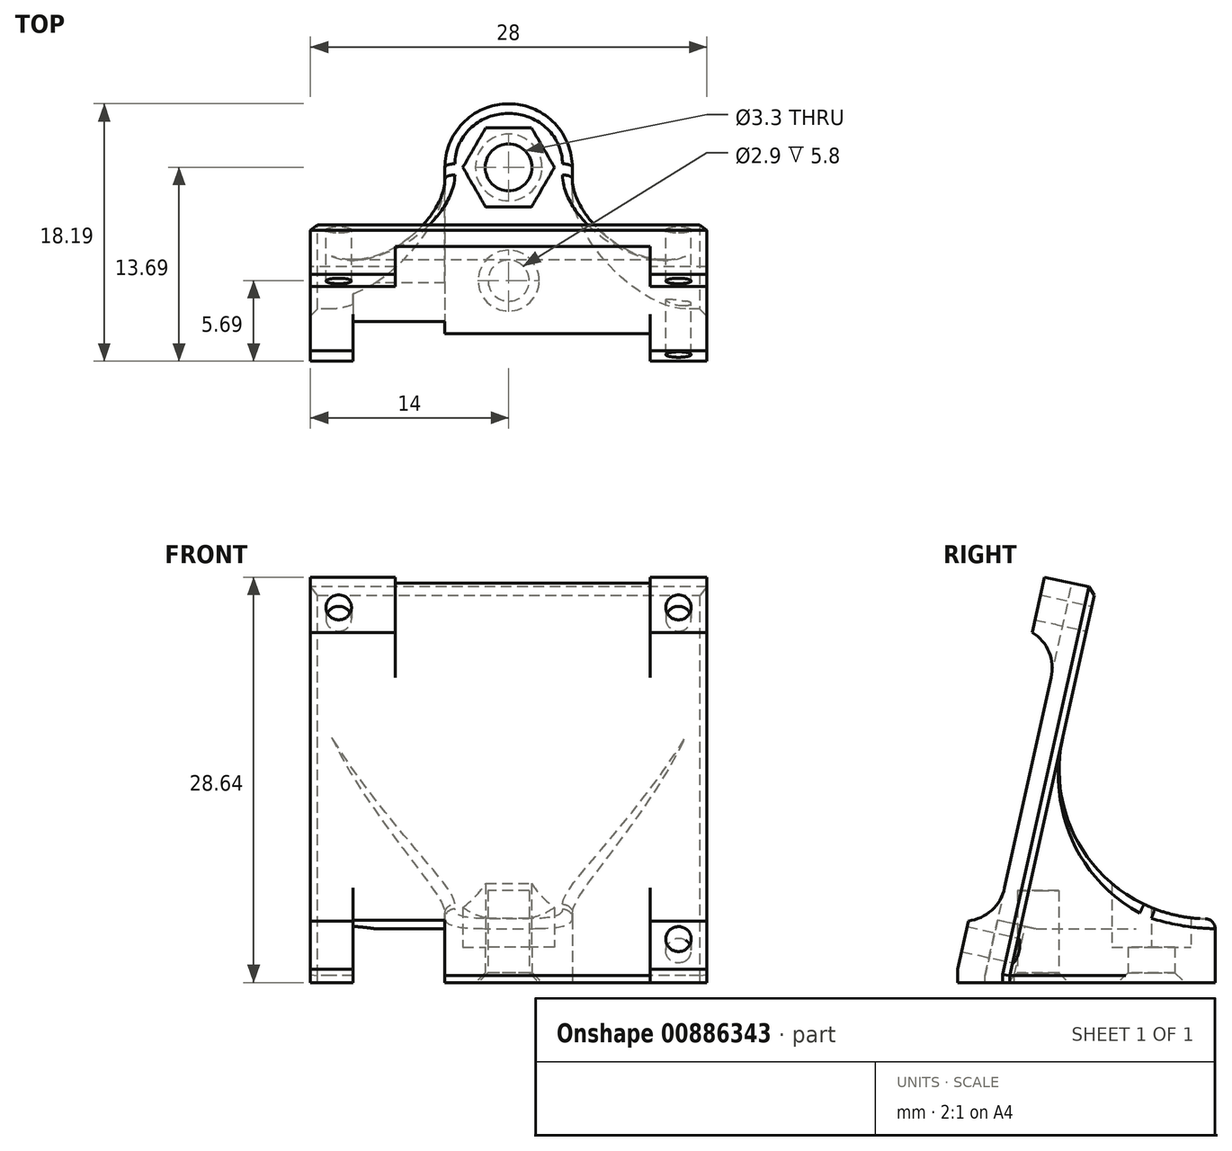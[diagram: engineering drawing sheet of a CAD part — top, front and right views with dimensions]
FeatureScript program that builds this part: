
annotation { "Feature Type Name" : "Feature", "Feature Type Description" : "" }
export const myFeature = defineFeature(function(context is Context, id is Id, definition is map)
    precondition{}
    {
        {
            var Q0;
            Q0=qCreatedBy(makeId("Top.planeOp"),FACE);
            var sketch = newSketch(context, id + "F0", { "sketchPlane" : qUnion([Q0])});
            skCircle(sketch, "E0", {"center": v(0, 0) * mm, "radius": 1.65 * mm});
            skCircle(sketch, "E1.cCircle", {"center": v(0, 0) * mm, "radius": 2.8 * mm, "construction": true});
            skLineSegment(sketch, "E1.0", {"start": v(-1.62, 2.8) * mm, "end": v(1.62, 2.8) * mm});
            skLineSegment(sketch, "E1.1", {"start": v(1.62, 2.8) * mm, "end": v(3.23, 0) * mm});
            skLineSegment(sketch, "E1.2", {"start": v(3.23, 0) * mm, "end": v(1.62, -2.8) * mm});
            skLineSegment(sketch, "E1.3", {"start": v(1.62, -2.8) * mm, "end": v(-1.62, -2.8) * mm});
            skLineSegment(sketch, "E1.4", {"start": v(-1.62, -2.8) * mm, "end": v(-3.23, 0) * mm});
            skLineSegment(sketch, "E1.5", {"start": v(-3.23, 0) * mm, "end": v(-1.62, 2.8) * mm});
            skPoint(sketch, "E1.0.midPoint", {"position": v(0, 2.8) * mm});
            skCircle(sketch, "E2", {"center": v(0, 0) * mm, "radius": 4.5 * mm});
            skLineSegment(sketch, "E3", {"start": v(-4.5, 0) * mm, "end": v(-4.5, -10) * mm});
            skLineSegment(sketch, "E4", {"start": v(-4.5, -10) * mm, "end": v(4.5, -10) * mm});
            skLineSegment(sketch, "E5", {"start": v(4.5, -10) * mm, "end": v(4.5, 0) * mm});
            skCircle(sketch, "E6", {"center": v(0, -8) * mm, "radius": 1.45 * mm});
            skSolve(sketch);
        }
        {
            var Q0;
            Q0 = qSketchRegion(id + "F0", true);
            var Q1;
            Q1=makeQuery(id+"F0.imprint","IMPRINT",FACE,{"disambiguationData":[TD([[makeQuery(id+"F0.imprint","IMPRINT",EDGE,{"derivedFrom":sQuery(id+"F0.wireOp",EDGE,"E0")}),-1.0]])]});
            var Q2;
            Q2=makeQuery(id+"F0.imprint","IMPRINT",FACE,{"disambiguationData":[TD([[makeQuery(id+"F0.imprint","IMPRINT",EDGE,{"derivedFrom":sQuery(id+"F0.wireOp",EDGE,"E6")}),1.0]])]});
            extrude(context, id + "F1", {"entities" : qUnion([Q0, Q1, Q2]), "depth" : 4 * mm, "offsetDistance" : 25 * mm});
        }
        {
            var Q0;
            Q0=qCreatedBy(makeId("Right.planeOp"),FACE);
            var sketch = newSketch(context, id + "F2", { "sketchPlane" : qUnion([Q0])});
            skPoint(sketch, "E7.0", {"position": v(-10, 0) * mm});
            skLineSegment(sketch, "E8", {"start": v(-10, 0) * mm, "end": v(-3.94, 27.34) * mm});
            skLineSegment(sketch, "E9", {"start": v(-3.94, 27.34) * mm, "end": v(-5.6, 27.7) * mm});
            skLineSegment(sketch, "E10", {"start": v(-5.6, 27.7) * mm, "end": v(-11.74, 0) * mm});
            skLineSegment(sketch, "E11", {"start": v(-11.74, 0) * mm, "end": v(-10, 0) * mm});
            skLineSegment(sketch, "E12", {"start": v(-11.74, 0) * mm, "end": v(-13.7, 0.43) * mm});
            skLineSegment(sketch, "E13", {"start": v(-13.7, 0.43) * mm, "end": v(-13.7, 0) * mm});
            skLineSegment(sketch, "E14", {"start": v(-13.7, 0) * mm, "end": v(-11.74, 0) * mm});
            skSolve(sketch);
        }
        {
            var Q0;
            Q0=makeQuery(id+"F2.imprint","IMPRINT",FACE,{"disambiguationData":[TD([[makeQuery(id+"F2.imprint","IMPRINT",EDGE,{"derivedFrom":sQuery(id+"F2.wireOp",EDGE,"E8")}),1.0]])]});
            extrude(context, id + "F3", {"entities" : qUnion([Q0]), "operationType" : NewBodyOperationType.ADD, "endBound" : BoundingType.SYMMETRIC, "depth" : 28 * mm, "offsetDistance" : 25 * mm});
        }
        {
            var Q0;
            Q0=makeQuery(id+"F0.imprint","IMPRINT",FACE,{"disambiguationData":[TD([[makeQuery(id+"F0.imprint","IMPRINT",EDGE,{"derivedFrom":sQuery(id+"F0.wireOp",EDGE,"E0")}),-1.0]])]});
            extrude(context, id + "F4", {"entities" : qUnion([Q0]), "operationType" : NewBodyOperationType.REMOVE, "endBound" : BoundingType.UP_TO_NEXT, "depth" : 6.3 * mm, "offsetDistance" : 25 * mm, "hasSecondDirection" : true, "secondDirectionOppositeDirection" : false, "secondDirectionDepth" : 2 * mm});
        }
        {
            var Q0;
            Q0=makeQuery(id+"F3.opExtrude","SWEPT_FACE",FACE,{"disambiguationData":[OSD([sQuery(id+"F2.wireOp",EDGE,"E10")])]});
            var sketch = newSketch(context, id + "F5", { "sketchPlane" : qUnion([Q0])});
            skLineSegment(sketch, "E15", {"start": v(14, 0.96) * mm, "end": v(10, 0.96) * mm});
            skLineSegment(sketch, "E16", {"start": v(10, 0.96) * mm, "end": v(10, -2.54) * mm});
            skLineSegment(sketch, "E17", {"start": v(-11, -2.54) * mm, "end": v(-11, 0.96) * mm});
            skLineSegment(sketch, "E18", {"start": v(-11, 0.96) * mm, "end": v(-14, 0.96) * mm});
            skLineSegment(sketch, "E19", {"start": v(-4.5, -2.54) * mm, "end": v(-4.5, 1.46) * mm});
            skLineSegment(sketch, "E20", {"start": v(-4.5, 1.46) * mm, "end": v(-11, 1.46) * mm});
            skLineSegment(sketch, "E21", {"start": v(-11, 1.46) * mm, "end": v(-11, 0.96) * mm});
            skLineSegment(sketch, "E22", {"start": v(14, 21.84) * mm, "end": v(10, 21.84) * mm});
            skLineSegment(sketch, "E23", {"start": v(10, 21.84) * mm, "end": v(10, 25.84) * mm});
            skLineSegment(sketch, "E24", {"start": v(-8, 21.84) * mm, "end": v(-8, 25.84) * mm});
            skLineSegment(sketch, "E25.trimOffspring", {"start": v(-8, 21.84) * mm, "end": v(-14, 21.84) * mm});
            skLineSegment(sketch, "E26", {"start": v(0, 25.84) * mm, "end": v(0, -2.54) * mm, "construction": true});
            skLineSegment(sketch, "E27", {"start": v(-14, 11.65) * mm, "end": v(14, 11.65) * mm, "construction": true});
            skPoint(sketch, "E28.middle", {"position": v(0, 11.65) * mm});
            skLineSegment(sketch, "E29.bottom", {"start": v(12, 23.65) * mm, "end": v(-12, 23.65) * mm, "construction": true});
            skLineSegment(sketch, "E29.top", {"start": v(12, -0.35) * mm, "end": v(-12, -0.35) * mm, "construction": true});
            skLineSegment(sketch, "E29.left", {"start": v(12, 23.65) * mm, "end": v(12, -0.35) * mm, "construction": true});
            skLineSegment(sketch, "E29.right", {"start": v(-12, 23.65) * mm, "end": v(-12, -0.35) * mm, "construction": true});
            skCircle(sketch, "E30", {"center": v(12, -0.35) * mm, "radius": 0.9 * mm});
            skCircle(sketch, "E31", {"center": v(12, 23.65) * mm, "radius": 0.9 * mm});
            skCircle(sketch, "E32", {"center": v(-12, 23.65) * mm, "radius": 0.9 * mm});
            skSolve(sketch);
        }
        {
            var Q0;
            {var subQ5=sQuery(id+"F5.wireOp",EDGE,"E24");Q0=makeQuery(id+"F5.imprint","IMPRINT",FACE,{"disambiguationData":[TD([[makeQuery(id+"F5.imprint","IMPRINT",EDGE,{"derivedFrom":subQ5}),1.0]])]});}
            var Q1;
            {var subQ5=sQuery(id+"F5.wireOp",EDGE,"E22");Q1=makeQuery(id+"F5.imprint","IMPRINT",FACE,{"disambiguationData":[TD([[makeQuery(id+"F5.imprint","IMPRINT",EDGE,{"derivedFrom":subQ5}),-1.0]])]});}
            var Q2;
            {var subQ5=sQuery(id+"F5.wireOp",EDGE,"E15");Q2=makeQuery(id+"F5.imprint","IMPRINT",FACE,{"disambiguationData":[TD([[makeQuery(id+"F5.imprint","IMPRINT",EDGE,{"derivedFrom":subQ5}),1.0]])]});}
            var Q3;
            {var subQ0=sQuery(id+"F5.wireOp",EDGE,"E17");Q3=makeQuery(id+"F5.imprint","IMPRINT",FACE,{"disambiguationData":[TD([[makeQuery(id+"F5.imprint","IMPRINT",EDGE,{"derivedFrom":subQ0}),1.0]])]});}
            extrude(context, id + "F6", {"entities" : qUnion([Q0, Q1, Q2, Q3]), "operationType" : NewBodyOperationType.ADD, "depth" : 2 * mm, "offsetDistance" : 25 * mm});
        }
        {
            var Q0;
            {var subQ1=sQuery(id+"F5.wireOp",EDGE,"E17");Q0=makeQuery(id+"F5.imprint","IMPRINT",FACE,{"disambiguationData":[TD([[makeQuery(id+"F5.imprint","IMPRINT",EDGE,{"derivedFrom":subQ1}),-1.0]])]});}
            extrude(context, id + "F7", {"entities" : qUnion([Q0]), "operationType" : NewBodyOperationType.REMOVE, "endBound" : BoundingType.UP_TO_NEXT, "oppositeDirection" : true, "depth" : 25 * mm, "offsetDistance" : 25 * mm});
        }
        {
            var Q0;
            Q0=makeQuery(id+"F3.boolean.opBoolean","INTERSECT",EDGE,{"derivedFrom":[makeQuery(id+"F1.opExtrude","SWEPT_FACE",FACE,{"disambiguationData":[OSD([sQuery(id+"F0.wireOp",EDGE,"E5")])]}),makeQuery(id+"F3.opExtrude","SWEPT_FACE",FACE,{"disambiguationData":[OSD([sQuery(id+"F2.wireOp",EDGE,"E8")])]})]});
            var Q1;
            Q1=makeQuery(id+"F3.boolean.opBoolean","INTERSECT",EDGE,{"derivedFrom":[makeQuery(id+"F1.opExtrude","SWEPT_FACE",FACE,{"disambiguationData":[OSD([sQuery(id+"F0.wireOp",EDGE,"E3")])]}),makeQuery(id+"F3.opExtrude","SWEPT_FACE",FACE,{"disambiguationData":[OSD([sQuery(id+"F2.wireOp",EDGE,"E8")])]})]});
            fillet(context, id + "F8", {"entities" : qUnion([Q0, Q1]), "radius" : 8 * mm, "tangentPropagation" : true, "rho" : 0.3, "crossSection" : FilletCrossSection.CONIC, "allowEdgeOverflow" : false});
        }
        {
            var Q0;
            Q0=makeQuery(id+"F5.imprint","IMPRINT",FACE,{"disambiguationData":[TD([[makeQuery(id+"F5.imprint","IMPRINT",EDGE,{"derivedFrom":sQuery(id+"F5.wireOp",EDGE,"E32")}),1.0]])]});
            var Q1;
            Q1=makeQuery(id+"F5.imprint","IMPRINT",FACE,{"disambiguationData":[TD([[makeQuery(id+"F5.imprint","IMPRINT",EDGE,{"derivedFrom":sQuery(id+"F5.wireOp",EDGE,"E31")}),1.0]])]});
            var Q2;
            Q2=makeQuery(id+"F5.imprint","IMPRINT",FACE,{"disambiguationData":[TD([[makeQuery(id+"F5.imprint","IMPRINT",EDGE,{"derivedFrom":sQuery(id+"F5.wireOp",EDGE,"E30")}),1.0]])]});
            extrude(context, id + "F9", {"entities" : qUnion([Q0, Q1, Q2]), "operationType" : NewBodyOperationType.REMOVE, "endBound" : BoundingType.UP_TO_NEXT, "oppositeDirection" : true, "depth" : 25 * mm, "offsetDistance" : 25 * mm});
        }
        {
            var Q0;
            Q0=makeQuery(id+"F3.boolean.opBoolean","INTERSECT",EDGE,{"derivedFrom":[makeQuery(id+"F1.opExtrude","CAP_FACE",FACE,{"disambiguationData":[OSD([sQuery(id+"F0.wireOp",EDGE,"E0"),sQuery(id+"F0.wireOp",EDGE,"E2"),sQuery(id+"F0.wireOp",EDGE,"E3"),sQuery(id+"F0.wireOp",EDGE,"E4"),sQuery(id+"F0.wireOp",EDGE,"E5")])],"isStart":false}),makeQuery(id+"F3.opExtrude","SWEPT_FACE",FACE,{"disambiguationData":[OSD([sQuery(id+"F2.wireOp",EDGE,"E8")])]})]});
            fillet(context, id + "F10", {"entities" : qUnion([Q0]), "radius" : 10.54 * mm, "tangentPropagation" : true, "allowEdgeOverflow" : false});
        }
        {
            var Q0;
            Q0=makeQuery(id+"F0.imprint","IMPRINT",FACE,{"disambiguationData":[TD([[makeQuery(id+"F0.imprint","IMPRINT",EDGE,{"derivedFrom":sQuery(id+"F0.wireOp",EDGE,"E6")}),1.0]])]});
            extrude(context, id + "F11", {"entities" : qUnion([Q0]), "operationType" : NewBodyOperationType.REMOVE, "depth" : 6 * mm, "offsetDistance" : 25 * mm});
        }
        {
            var Q0;
            Q0=makeQuery(id+"F6.opExtrude","CAP_EDGE",EDGE,{"disambiguationData":[OSD([sQuery(id+"F5.wireOp",EDGE,"E22")])],"isStart":true});
            var Q1;
            Q1=makeQuery(id+"F6.opExtrude","CAP_EDGE",EDGE,{"disambiguationData":[OSD([sQuery(id+"F5.wireOp",EDGE,"E25.trimOffspring")])],"isStart":true});
            var Q2;
            Q2=makeQuery(id+"F6.opExtrude","CAP_EDGE",EDGE,{"disambiguationData":[OSD([sQuery(id+"F5.wireOp",EDGE,"E15")])],"isStart":true});
            var Q3;
            Q3=makeQuery(id+"F6.opExtrude","CAP_EDGE",EDGE,{"disambiguationData":[OSD([sQuery(id+"F5.wireOp",EDGE,"E18")])],"isStart":true});
            fillet(context, id + "F12", {"entities" : qUnion([Q0, Q1, Q2, Q3]), "radius" : 3 * mm, "tangentPropagation" : true, "allowEdgeOverflow" : false});
        }
        {
            var Q0;
            Q0=makeQuery(id+"F2.imprint","IMPRINT",FACE,{"disambiguationData":[TD([[makeQuery(id+"F2.imprint","IMPRINT",EDGE,{"derivedFrom":sQuery(id+"F2.wireOp",EDGE,"E12")}),1.0]])]});
            extrude(context, id + "F13", {"entities" : qUnion([Q0]), "operationType" : NewBodyOperationType.ADD, "depth" : 14 * mm, "offsetDistance" : 25 * mm, "hasSecondDirection" : true, "secondDirectionOppositeDirection" : false, "secondDirectionDepth" : 10 * mm});
        }
        {
            var Q0;
            Q0=makeQuery(id+"F2.imprint","IMPRINT",FACE,{"disambiguationData":[TD([[makeQuery(id+"F2.imprint","IMPRINT",EDGE,{"derivedFrom":sQuery(id+"F2.wireOp",EDGE,"E12")}),1.0]])]});
            extrude(context, id + "F14", {"entities" : qUnion([Q0]), "operationType" : NewBodyOperationType.ADD, "oppositeDirection" : true, "depth" : 14 * mm, "offsetDistance" : 25 * mm, "hasSecondDirection" : true, "secondDirectionOppositeDirection" : true, "secondDirectionDepth" : 11 * mm});
        }
        {
            var Q0;
            {var subQ0=sQuery(id+"F2.wireOp",EDGE,"E8");var subQ1=sQuery(id+"F0.wireOp",EDGE,"E5");Q0=makeQuery(id+"F10.opFillet","BLEND_EDGE",EDGE,{"blendedFrom":[makeQuery(id+"F3.boolean.opBoolean","INTERSECT",EDGE,{"derivedFrom":[makeQuery(id+"F1.opExtrude","CAP_FACE",FACE,{"disambiguationData":[OSD([sQuery(id+"F0.wireOp",EDGE,"E0"),sQuery(id+"F0.wireOp",EDGE,"E2"),sQuery(id+"F0.wireOp",EDGE,"E3"),sQuery(id+"F0.wireOp",EDGE,"E4"),subQ1])],"isStart":false}),makeQuery(id+"F3.opExtrude","SWEPT_FACE",FACE,{"disambiguationData":[OSD([subQ0])]})]}),makeQuery(id+"F8.opFillet","BLEND_FACE",FACE,{"disambiguationData":[OSD([subQ1,subQ0]),OD(0.0)]})],"blendedInto":[makeQuery(id+"F8.opFillet","BLEND_FACE",FACE,{"disambiguationData":[OSD([subQ1,subQ0]),OD(0.0)]})]});}
            fillet(context, id + "F15", {"entities" : qUnion([Q0]), "radius" : 0.7 * mm, "tangentPropagation" : true, "allowEdgeOverflow" : false});
        }
        {
            var Q0;
            {var subQ0=sQuery(id+"F2.wireOp",EDGE,"E14");var subQ3=sQuery(id+"F0.wireOp",EDGE,"E3");var subQ4=sQuery(id+"F0.wireOp",EDGE,"E0");var subQ7=sQuery(id+"F2.wireOp",EDGE,"E11");var subQ12=sQuery(id+"F0.wireOp",EDGE,"E5");var subQ13=sQuery(id+"F0.wireOp",EDGE,"E2");Q0=makeQuery(id+"F13.boolean.opBoolean","MERGE",FACE,{"derivedFrom":[makeQuery(id+"F7.boolean.opBoolean","SPLIT",FACE,{"disambiguationData":[TD([makeQuery(id+"F1.opExtrude","SWEPT_FACE",FACE,{"disambiguationData":[OSD([subQ4])]})])],"derivedFrom":makeQuery(id+"F3.boolean.opBoolean","MERGE",FACE,{"derivedFrom":[makeQuery(id+"F1.opExtrude","CAP_FACE",FACE,{"disambiguationData":[OSD([subQ4,subQ13,subQ3,sQuery(id+"F0.wireOp",EDGE,"E4"),subQ12])],"isStart":true}),makeQuery(id+"F3.opExtrude","SWEPT_FACE",FACE,{"disambiguationData":[OSD([subQ7])]})]})}),makeQuery(id+"F13.opExtrude","SWEPT_FACE",FACE,{"disambiguationData":[OSD([subQ0])]})]});}
            var Q1;
            {var subQ0=sQuery(id+"F2.wireOp",EDGE,"E14");var subQ4=sQuery(id+"F2.wireOp",EDGE,"E11");var subQ7=sQuery(id+"F5.wireOp",EDGE,"E17");Q1=makeQuery(id+"F14.boolean.opBoolean","MERGE",FACE,{"derivedFrom":[makeQuery(id+"F7.boolean.opBoolean","SPLIT",FACE,{"disambiguationData":[TD([makeQuery(id+"F6.opExtrude","SWEPT_FACE",FACE,{"disambiguationData":[OSD([subQ7])]})])],"derivedFrom":makeQuery(id+"F3.boolean.opBoolean","MERGE",FACE,{"derivedFrom":[makeQuery(id+"F1.opExtrude","CAP_FACE",FACE,{"disambiguationData":[OSD([sQuery(id+"F0.wireOp",EDGE,"E0"),sQuery(id+"F0.wireOp",EDGE,"E2"),sQuery(id+"F0.wireOp",EDGE,"E3"),sQuery(id+"F0.wireOp",EDGE,"E4"),sQuery(id+"F0.wireOp",EDGE,"E5")])],"isStart":true}),makeQuery(id+"F3.opExtrude","SWEPT_FACE",FACE,{"disambiguationData":[OSD([subQ4])]})]})}),makeQuery(id+"F14.opExtrude","SWEPT_FACE",FACE,{"disambiguationData":[OSD([subQ0])]})]});}
            extrude(context, id + "F16", {"entities" : qUnion([Q0, Q1]), "operationType" : NewBodyOperationType.ADD, "depth" : 0.5 * mm, "offsetDistance" : 25 * mm});
        }
        {
            var Q0;
            Q0=makeQuery(id+"F16.opExtrude","CAP_EDGE",EDGE,{"disambiguationData":[OSD([sQuery(id+"F0.wireOp",EDGE,"E0")])],"isStart":false});
            var Q1;
            Q1=makeQuery(id+"F16.opExtrude","CAP_EDGE",EDGE,{"disambiguationData":[OSD([sQuery(id+"F0.wireOp",EDGE,"E6")])],"isStart":false});
            chamfer(context, id + "F17", {"entities" : qUnion([Q0, Q1]), "width" : 0.7 * mm, "tangentPropagation" : true});
        }
        {
            var Q0;
            Q0=makeQuery(id+"F3.opExtrude","CAP_EDGE",EDGE,{"disambiguationData":[OSD([sQuery(id+"F2.wireOp",EDGE,"E8")])],"isStart":false});
            var Q1;
            Q1=makeQuery(id+"F3.opExtrude","SWEPT_EDGE",EDGE,{"disambiguationData":[OSD([sQuery(id+"F2.wireOp",EDGE,"E8"),sQuery(id+"F2.wireOp",EDGE,"E9")])]});
            var Q2;
            Q2=makeQuery(id+"F3.opExtrude","CAP_EDGE",EDGE,{"disambiguationData":[OSD([sQuery(id+"F2.wireOp",EDGE,"E8")])],"isStart":true});
            var Q3;
            {var subQ0=sQuery(id+"F2.wireOp",EDGE,"E11");var subQ1=sQuery(id+"F2.wireOp",EDGE,"E8");Q3=makeQuery(id+"F16.opExtrude","SWEPT_EDGE",EDGE,{"disambiguationData":[OSD([subQ1,subQ0]),TDD([makeQuery(id+"F3.opExtrude","CAP_VERTEX",VERTEX,{"disambiguationData":[OSD([subQ1,subQ0])],"isStart":true})])]});}
            var Q4;
            {var subQ0=sQuery(id+"F2.wireOp",EDGE,"E11");var subQ1=sQuery(id+"F2.wireOp",EDGE,"E8");Q4=makeQuery(id+"F16.opExtrude","SWEPT_EDGE",EDGE,{"disambiguationData":[OSD([subQ1,subQ0]),TDD([makeQuery(id+"F3.opExtrude","CAP_VERTEX",VERTEX,{"disambiguationData":[OSD([subQ1,subQ0])],"isStart":false})])]});}
            chamfer(context, id + "F18", {"entities" : qUnion([Q0, Q1, Q2, Q3, Q4]), "width" : 0.5 * mm, "tangentPropagation" : true});
        }
        {
            var Q0;
            Q0=qCreatedBy(makeId("Front.planeOp"),FACE);
            var sketch = newSketch(context, id + "F19", { "sketchPlane" : qUnion([Q0])});
            skLineSegment(sketch, "E33.0", {"start": v(-4.5, 0) * mm, "end": v(-4.5, 3.3) * mm});
            skLineSegment(sketch, "E34.0", {"start": v(-11, 0) * mm, "end": v(-11, 3.3) * mm});
            skPoint(sketch, "E35.0", {"position": v(0.01, 3.3) * mm});
            skLineSegment(sketch, "E36", {"start": v(-4.5, 3.3) * mm, "end": v(-11, 3.3) * mm});
            skPoint(sketch, "E37.0.end.orphan", {"position": v(-11, 3.42) * mm});
            skPoint(sketch, "E37.0.start.orphan", {"position": v(-11, 3.9) * mm});
            skPoint(sketch, "E38.orphan", {"position": v(-4.5, 3.9) * mm});
            skLineSegment(sketch, "E39", {"start": v(-4.5, 0) * mm, "end": v(-11, 0) * mm});
            skSolve(sketch);
        }
        {
            var Q0;
            Q0 = qSketchRegion(id + "F19", true);
            extrude(context, id + "F20", {"entities" : qUnion([Q0]), "operationType" : NewBodyOperationType.REMOVE, "endBound" : BoundingType.THROUGH_ALL, "depth" : 51.8 * mm, "offsetDistance" : 25 * mm});
        }
    });
